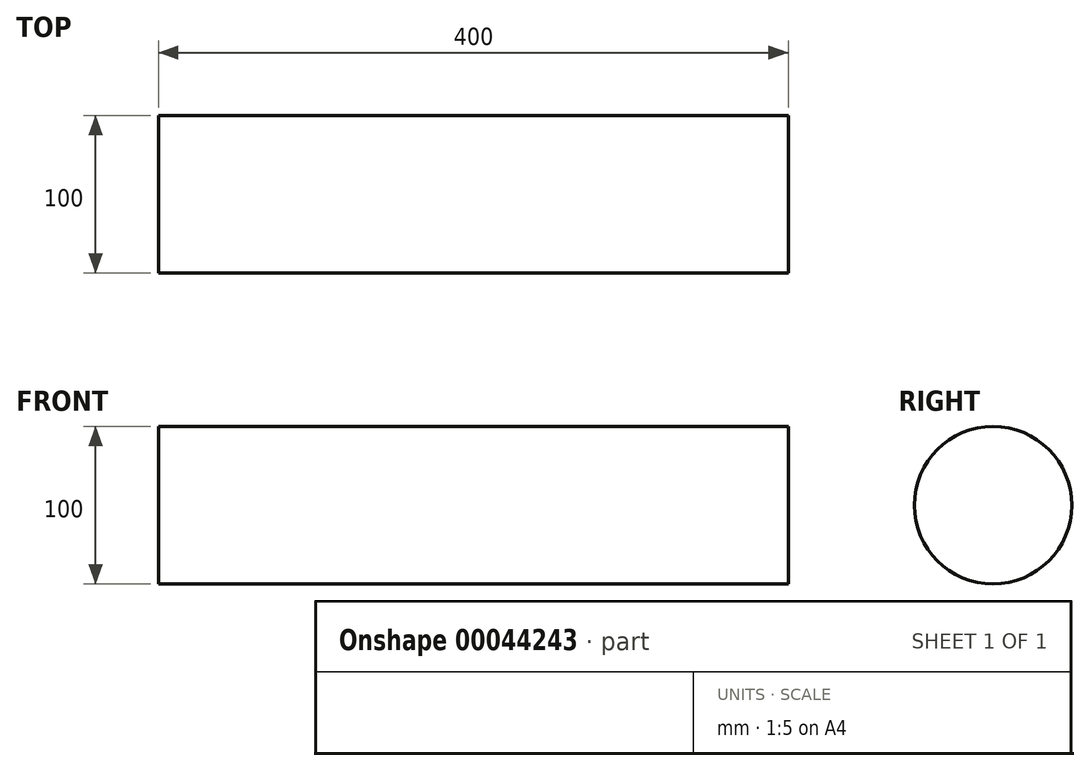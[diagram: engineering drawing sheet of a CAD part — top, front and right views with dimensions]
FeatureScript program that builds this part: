
annotation { "Feature Type Name" : "Feature", "Feature Type Description" : "" }
export const myFeature = defineFeature(function(context is Context, id is Id, definition is map)
    precondition{}
    {
        {
            var Q0;
            Q0=qCreatedBy(makeId("Right.planeOp"),FACE);
            var sketch = newSketch(context, id + "F0", { "sketchPlane" : qUnion([Q0])});
            skCircle(sketch, "E0", {"center": v(0, 0) * mm, "radius": 50 * mm});
            skSolve(sketch);
        }
        {
            var Q0;
            Q0=makeQuery(id+"F0.imprint","IMPRINT",FACE,{"disambiguationData":[TD([[makeQuery(id+"F0.imprint","IMPRINT",EDGE,{"derivedFrom":sQuery(id+"F0.wireOp",EDGE,"E0")}),1.0]])]});
            extrude(context, id + "F1", {"entities" : qUnion([Q0]), "depth" : 400 * mm});
        }
    });
